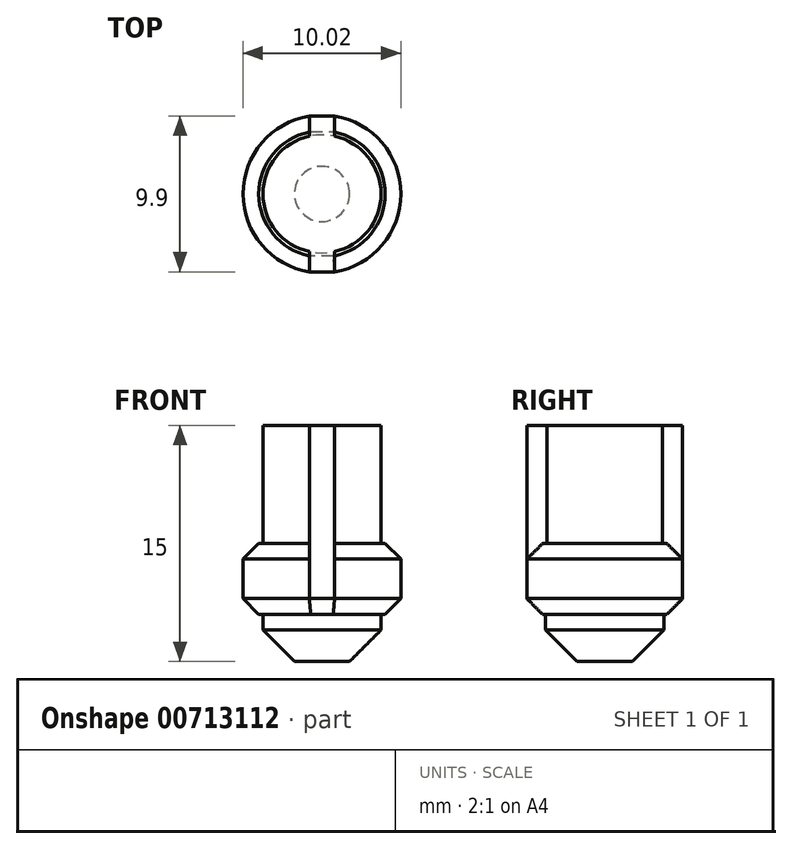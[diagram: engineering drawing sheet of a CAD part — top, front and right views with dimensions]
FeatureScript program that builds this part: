
annotation { "Feature Type Name" : "Feature", "Feature Type Description" : "" }
export const myFeature = defineFeature(function(context is Context, id is Id, definition is map)
    precondition{}
    {
        {
            var Q0;
            Q0=qCreatedBy(makeId("Top.planeOp"),FACE);
            var sketch = newSketch(context, id + "F0", { "sketchPlane" : qUnion([Q0])});
            skCircle(sketch, "E0", {"center": v(0, 0) * mm, "radius": 3.75 * mm});
            skLineSegment(sketch, "E1.bottom", {"start": v(0.8, 4.95) * mm, "end": v(-0.8, 4.95) * mm});
            skLineSegment(sketch, "E1.top", {"start": v(0.8, -4.95) * mm, "end": v(-0.8, -4.95) * mm});
            skLineSegment(sketch, "E1.left", {"start": v(0.8, 4.95) * mm, "end": v(0.8, -4.95) * mm});
            skLineSegment(sketch, "E1.right", {"start": v(-0.8, 4.95) * mm, "end": v(-0.8, -4.95) * mm});
            skCircle(sketch, "E2", {"center": v(0, 0) * mm, "radius": 5.01 * mm});
            skSolve(sketch);
        }
        {
            var Q0;
            {var subQ0=sQuery(id+"F0.wireOp",EDGE,"E1.left");var subQ1=sQuery(id+"F0.wireOp",EDGE,"E0");var subQ2=makeQuery(id+"F0.imprint","INTERSECT",VERTEX,{"disambiguationData":[OD(0.0)],"derivedFrom":[subQ1,subQ0]});Q0=makeQuery(id+"F0.imprint","IMPRINT",FACE,{"disambiguationData":[TD([[makeQuery(id+"F0.imprint","IMPRINT",EDGE,{"disambiguationData":[TD([[subQ2,1.0]])],"derivedFrom":subQ1}),1.0]])]});}
            var Q1;
            {var subQ0=sQuery(id+"F0.wireOp",EDGE,"E1.right");var subQ1=sQuery(id+"F0.wireOp",EDGE,"E0");var subQ2=makeQuery(id+"F0.imprint","INTERSECT",VERTEX,{"disambiguationData":[OD(0.0)],"derivedFrom":[subQ1,subQ0]});Q1=makeQuery(id+"F0.imprint","IMPRINT",FACE,{"disambiguationData":[TD([[makeQuery(id+"F0.imprint","IMPRINT",EDGE,{"disambiguationData":[TD([[subQ2,1.0]])],"derivedFrom":subQ1}),1.0]])]});}
            var Q2;
            {var subQ0=sQuery(id+"F0.wireOp",EDGE,"E1.right");var subQ1=sQuery(id+"F0.wireOp",EDGE,"E0");var subQ2=makeQuery(id+"F0.imprint","INTERSECT",VERTEX,{"disambiguationData":[OD(0.0)],"derivedFrom":[subQ1,subQ0]});Q2=makeQuery(id+"F0.imprint","IMPRINT",FACE,{"disambiguationData":[TD([[makeQuery(id+"F0.imprint","IMPRINT",EDGE,{"disambiguationData":[TD([[subQ2,-1.0]])],"derivedFrom":subQ1}),1.0]])]});}
            extrude(context, id + "F1", {"entities" : qUnion([Q0, Q1, Q2]), "oppositeDirection" : true, "depth" : 7.5 * mm, "offsetDistance" : 25 * mm});
        }
        {
            var Q0;
            {var subQ0=sQuery(id+"F0.wireOp",EDGE,"E1.left");var subQ1=sQuery(id+"F0.wireOp",EDGE,"E0");var subQ2=makeQuery(id+"F0.imprint","INTERSECT",VERTEX,{"disambiguationData":[OD(0.0)],"derivedFrom":[subQ1,subQ0]});Q0=makeQuery(id+"F0.imprint","IMPRINT",FACE,{"disambiguationData":[TD([[makeQuery(id+"F0.imprint","IMPRINT",EDGE,{"disambiguationData":[TD([[subQ2,1.0]])],"derivedFrom":subQ1}),1.0]])]});}
            var Q1;
            {var subQ0=sQuery(id+"F0.wireOp",EDGE,"E1.right");var subQ1=sQuery(id+"F0.wireOp",EDGE,"E0");var subQ2=makeQuery(id+"F0.imprint","INTERSECT",VERTEX,{"disambiguationData":[OD(0.0)],"derivedFrom":[subQ1,subQ0]});Q1=makeQuery(id+"F0.imprint","IMPRINT",FACE,{"disambiguationData":[TD([[makeQuery(id+"F0.imprint","IMPRINT",EDGE,{"disambiguationData":[TD([[subQ2,1.0]])],"derivedFrom":subQ1}),1.0]])]});}
            var Q2;
            {var subQ0=sQuery(id+"F0.wireOp",EDGE,"E1.right");var subQ1=sQuery(id+"F0.wireOp",EDGE,"E0");var subQ2=makeQuery(id+"F0.imprint","INTERSECT",VERTEX,{"disambiguationData":[OD(0.0)],"derivedFrom":[subQ1,subQ0]});Q2=makeQuery(id+"F0.imprint","IMPRINT",FACE,{"disambiguationData":[TD([[makeQuery(id+"F0.imprint","IMPRINT",EDGE,{"disambiguationData":[TD([[subQ2,-1.0]])],"derivedFrom":subQ1}),1.0]])]});}
            var Q3;
            {var subQ5=sQuery(id+"F0.wireOp",EDGE,"E1.bottom");Q3=makeQuery(id+"F0.imprint","IMPRINT",FACE,{"disambiguationData":[TD([[makeQuery(id+"F0.imprint","IMPRINT",EDGE,{"derivedFrom":subQ5}),1.0]])]});}
            var Q4;
            {var subQ5=sQuery(id+"F0.wireOp",EDGE,"E1.top");Q4=makeQuery(id+"F0.imprint","IMPRINT",FACE,{"disambiguationData":[TD([[makeQuery(id+"F0.imprint","IMPRINT",EDGE,{"derivedFrom":subQ5}),-1.0]])]});}
            extrude(context, id + "F2", {"entities" : qUnion([Q0, Q1, Q2, Q3, Q4]), "operationType" : NewBodyOperationType.ADD, "depth" : 7.5 * mm, "offsetDistance" : 25 * mm});
        }
        {
            var Q0;
            {var subQ0=sQuery(id+"F0.wireOp",EDGE,"E1.left");var subQ1=sQuery(id+"F0.wireOp",EDGE,"E0");var subQ2=makeQuery(id+"F0.imprint","INTERSECT",VERTEX,{"disambiguationData":[OD(0.0)],"derivedFrom":[subQ1,subQ0]});Q0=makeQuery(id+"F0.imprint","IMPRINT",FACE,{"disambiguationData":[TD([[makeQuery(id+"F0.imprint","IMPRINT",EDGE,{"disambiguationData":[TD([[subQ2,1.0]])],"derivedFrom":subQ1}),-1.0]])]});}
            var Q1;
            {var subQ5=sQuery(id+"F0.wireOp",EDGE,"E1.top");Q1=makeQuery(id+"F0.imprint","IMPRINT",FACE,{"disambiguationData":[TD([[makeQuery(id+"F0.imprint","IMPRINT",EDGE,{"derivedFrom":subQ5}),-1.0]])]});}
            var Q2;
            {var subQ0=sQuery(id+"F0.wireOp",EDGE,"E1.right");var subQ1=sQuery(id+"F0.wireOp",EDGE,"E0");var subQ2=makeQuery(id+"F0.imprint","INTERSECT",VERTEX,{"disambiguationData":[OD(0.0)],"derivedFrom":[subQ1,subQ0]});Q2=makeQuery(id+"F0.imprint","IMPRINT",FACE,{"disambiguationData":[TD([[makeQuery(id+"F0.imprint","IMPRINT",EDGE,{"disambiguationData":[TD([[subQ2,-1.0]])],"derivedFrom":subQ1}),-1.0]])]});}
            var Q3;
            {var subQ5=sQuery(id+"F0.wireOp",EDGE,"E1.bottom");Q3=makeQuery(id+"F0.imprint","IMPRINT",FACE,{"disambiguationData":[TD([[makeQuery(id+"F0.imprint","IMPRINT",EDGE,{"derivedFrom":subQ5}),1.0]])]});}
            extrude(context, id + "F3", {"entities" : qUnion([Q0, Q1, Q2, Q3]), "operationType" : NewBodyOperationType.ADD, "oppositeDirection" : true, "depth" : 4.5 * mm, "offsetDistance" : 25 * mm});
        }
        {
            var Q0;
            Q0=makeQuery(id+"F1.opExtrude","CAP_FACE",FACE,{"disambiguationData":[OSD([sQuery(id+"F0.wireOp",EDGE,"E0")])],"isStart":false});
            chamfer(context, id + "F4", {"entities" : qUnion([Q0]), "width" : 2 * mm, "tangentPropagation" : true});
        }
        {
            var Q0;
            {var subQ0=sQuery(id+"F0.wireOp",EDGE,"E2");var subQ1=sQuery(id+"F0.wireOp",EDGE,"E1.right");Q0=makeQuery(id+"F3.opExtrude","CAP_EDGE",EDGE,{"disambiguationData":[OSD([subQ0]),TDD([makeQuery(id+"F0.imprint","IMPRINT",EDGE,{"disambiguationData":[TD([[makeQuery(id+"F0.imprint","INTERSECT",VERTEX,{"derivedFrom":[sQuery(id+"F0.wireOp",EDGE,"E1.bottom"),subQ1,subQ0]}),-1.0]])],"derivedFrom":subQ0})])],"isStart":false});}
            var Q1;
            {var subQ0=sQuery(id+"F0.wireOp",EDGE,"E2");var subQ1=sQuery(id+"F0.wireOp",EDGE,"E1.left");Q1=makeQuery(id+"F3.opExtrude","CAP_EDGE",EDGE,{"disambiguationData":[OSD([subQ0]),TDD([makeQuery(id+"F0.imprint","IMPRINT",EDGE,{"disambiguationData":[TD([[makeQuery(id+"F0.imprint","INTERSECT",VERTEX,{"derivedFrom":[sQuery(id+"F0.wireOp",EDGE,"E1.bottom"),subQ1,subQ0]}),1.0]])],"derivedFrom":subQ0})])],"isStart":false});}
            var Q2;
            Q2=makeQuery(id+"F3.opExtrude","CAP_EDGE",EDGE,{"disambiguationData":[OSD([sQuery(id+"F0.wireOp",EDGE,"E1.top")])],"isStart":false});
            var Q3;
            Q3=makeQuery(id+"F3.opExtrude","CAP_EDGE",EDGE,{"disambiguationData":[OSD([sQuery(id+"F0.wireOp",EDGE,"E1.bottom")])],"isStart":false});
            var Q4;
            {var subQ0=sQuery(id+"F0.wireOp",EDGE,"E2");var subQ1=sQuery(id+"F0.wireOp",EDGE,"E1.right");Q4=makeQuery(id+"F3.opExtrude","CAP_EDGE",EDGE,{"disambiguationData":[OSD([subQ0]),TDD([makeQuery(id+"F0.imprint","IMPRINT",EDGE,{"disambiguationData":[TD([[makeQuery(id+"F0.imprint","INTERSECT",VERTEX,{"derivedFrom":[sQuery(id+"F0.wireOp",EDGE,"E1.bottom"),subQ1,subQ0]}),-1.0]])],"derivedFrom":subQ0})])],"isStart":true});}
            var Q5;
            {var subQ0=sQuery(id+"F0.wireOp",EDGE,"E2");var subQ1=sQuery(id+"F0.wireOp",EDGE,"E1.left");Q5=makeQuery(id+"F3.opExtrude","CAP_EDGE",EDGE,{"disambiguationData":[OSD([subQ0]),TDD([makeQuery(id+"F0.imprint","IMPRINT",EDGE,{"disambiguationData":[TD([[makeQuery(id+"F0.imprint","INTERSECT",VERTEX,{"derivedFrom":[sQuery(id+"F0.wireOp",EDGE,"E1.bottom"),subQ1,subQ0]}),1.0]])],"derivedFrom":subQ0})])],"isStart":true});}
            chamfer(context, id + "F5", {"entities" : qUnion([Q0, Q1, Q2, Q3, Q4, Q5]), "width" : 1 * mm, "tangentPropagation" : true});
        }
    });
